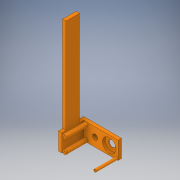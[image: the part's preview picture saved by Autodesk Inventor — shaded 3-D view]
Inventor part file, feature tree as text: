
AUTODESK INVENTOR PART (.ipt)
format: ipt  version: 2017 (Build 210142000, 142)  size: 217,600 bytes
history: native  units: in
note: dims shown in document units (in); Inventor stores cm internally (conversion verified against a paired STEP export)
features: extrude x12, sketch x12
ambient origin geometry x8: Origin, YZ Plane, XZ Plane, XY Plane, X Axis, Y Axis, Z Axis, Center Point
bodies: Solid1 (feature_tree)
feature tree (24):
  extrude  "Extrusion1"  Depth=1.3in
  extrude  "Extrusion2"  Depth=0.25in
  extrude  "Extrusion3"  Depth=1.05in
  extrude  "Extrusion4"  Depth=1.0in
  extrude  "Extrusion14"  Depth=0.5in
  extrude  "Extrusion15"  Depth=0.3in
  extrude  "Extrusion16"  Depth=0.3in TaperAngle=0.0deg
  extrude  "Extrusion17"  Depth=0.15in
  extrude  "Extrusion18"  Depth=0.15in
  extrude  "Extrusion20"  Depth=0.3in
  extrude  "Extrusion21"  Depth=0.3in
  extrude  "Extrusion23"  Depth=1.5in TaperAngle=0.0deg
  sketch  "Sketch1"  dims[d0=2.0in d1=1.3in]
  sketch  "Sketch2"  dims[d2=0.25in d3=0.0in d4=0.65in]
  sketch  "Sketch3"  dims[d5=0.65in d6=1.05in]
  sketch  "Sketch4"  dims[d7=0.3in d8=1.0in]
  sketch  "Sketch14"  dims[d9=0.2in d10=0.0in d11=0.5in]
  sketch  "Sketch15"  dims[d12=0.2in d13=0.0in d14=0.3in]
  sketch  "Sketch16"  dims[d15=0.4in d16=0.3in d17=0.0in]
  sketch  "Sketch17"  dims[d56=0.5in d57=0.0in d58=0.15in]
  sketch  "Sketch18"  dims[d59=0.15in d60=0.15in]
  sketch  "Sketch20"  dims[d61=0.15in d62=0.3in]
  sketch  "Sketch21"  dims[d63=0.3in d64=0.13in]
  sketch  "Sketch23"  dims[d65=0.13in d66=1.5in d67=0.0in d68=0.2in d69=0.1in d70=0.1in d71=0.13in d72=1.5in d73=0.0in d74=0.13in d75=0.3in d76=0.13in d77=0.3in d78=0.2in d79=0.1in d80=0.0in d81=0.5in d82=0.0in d86=0.2in d87=0.0in d88=0.25in d89=1.3in d90=1.6in d91=0.0in d94=1.0in d95=0.25in d96=0.3in d97=7.0in d98=0.0in]
